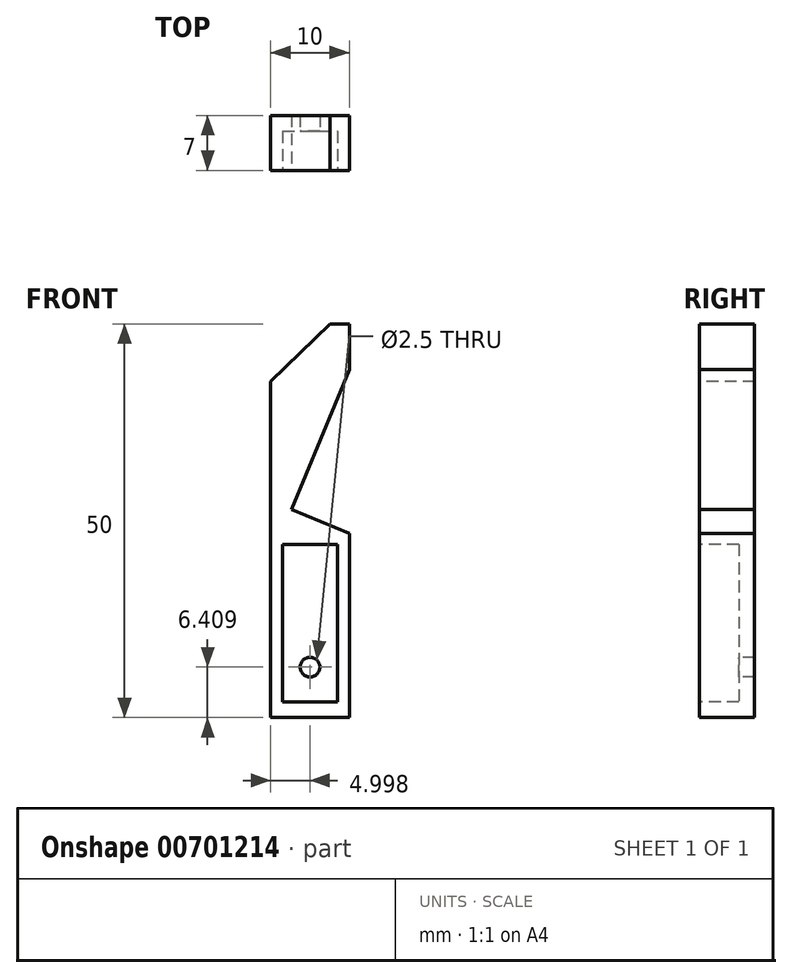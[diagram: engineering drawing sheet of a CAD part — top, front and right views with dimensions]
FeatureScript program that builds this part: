
annotation { "Feature Type Name" : "Feature", "Feature Type Description" : "" }
export const myFeature = defineFeature(function(context is Context, id is Id, definition is map)
    precondition{}
    {
        {
            var Q0;
            Q0=qCreatedBy(makeId("Front.planeOp"),FACE);
            var sketch = newSketch(context, id + "F0", { "sketchPlane" : qUnion([Q0])});
            skLineSegment(sketch, "E0.bottom", {"start": v(-32.17, 52.44) * mm, "end": v(-22.17, 52.44) * mm});
            skLineSegment(sketch, "E0.top", {"start": v(-32.17, 2.44) * mm, "end": v(-22.17, 2.44) * mm});
            skLineSegment(sketch, "E0.left", {"start": v(-32.17, 52.44) * mm, "end": v(-32.17, 2.44) * mm});
            skLineSegment(sketch, "E0.right", {"start": v(-22.17, 52.44) * mm, "end": v(-22.17, 2.44) * mm});
            skSolve(sketch);
        }
        {
            var Q0;
            Q0 = qSketchRegion(id + "F0", true);
            extrude(context, id + "F1", {"entities" : qUnion([Q0]), "depth" : 7 * mm, "offsetDistance" : 25 * mm});
        }
        {
            var Q0;
            Q0=makeQuery(id+"F1.opExtrude","CAP_FACE",FACE,{"disambiguationData":[OSD([sQuery(id+"F0.wireOp",EDGE,"E0.bottom"),sQuery(id+"F0.wireOp",EDGE,"E0.top"),sQuery(id+"F0.wireOp",EDGE,"E0.left"),sQuery(id+"F0.wireOp",EDGE,"E0.right")])],"isStart":false});
            var sketch = newSketch(context, id + "F2", { "sketchPlane" : qUnion([Q0])});
            skLineSegment(sketch, "E1.bottom", {"start": v(-30.67, 24.44) * mm, "end": v(-23.67, 24.44) * mm});
            skLineSegment(sketch, "E1.top", {"start": v(-30.67, 4.44) * mm, "end": v(-23.67, 4.44) * mm});
            skLineSegment(sketch, "E1.left", {"start": v(-30.67, 24.44) * mm, "end": v(-30.67, 4.44) * mm});
            skLineSegment(sketch, "E1.right", {"start": v(-23.67, 24.44) * mm, "end": v(-23.67, 4.44) * mm});
            skSolve(sketch);
        }
        {
            var Q0;
            Q0 = qSketchRegion(id + "F2", true);
            extrude(context, id + "F3", {"entities" : qUnion([Q0]), "operationType" : NewBodyOperationType.REMOVE, "oppositeDirection" : true, "depth" : 5 * mm, "offsetDistance" : 25 * mm});
        }
        {
            var Q0;
            Q0=makeQuery(id+"F3.boolean.opBoolean","COPY",FACE,{"derivedFrom":makeQuery(id+"F3.opExtrude","CAP_FACE",FACE,{"disambiguationData":[OSD([sQuery(id+"F2.wireOp",EDGE,"E1.bottom"),sQuery(id+"F2.wireOp",EDGE,"E1.top"),sQuery(id+"F2.wireOp",EDGE,"E1.left"),sQuery(id+"F2.wireOp",EDGE,"E1.right")])],"isStart":false})});
            var sketch = newSketch(context, id + "F4", { "sketchPlane" : qUnion([Q0])});
            skCircle(sketch, "E2", {"center": v(-27.17, 8.85) * mm, "radius": 1.25 * mm});
            skSolve(sketch);
        }
        {
            var Q0;
            Q0 = qSketchRegion(id + "F4", true);
            extrude(context, id + "F5", {"entities" : qUnion([Q0]), "operationType" : NewBodyOperationType.REMOVE, "endBound" : BoundingType.THROUGH_ALL, "oppositeDirection" : true, "depth" : 25 * mm, "offsetDistance" : 25 * mm});
        }
        {
            var Q0;
            Q0=makeQuery(id+"F1.opExtrude","CAP_FACE",FACE,{"disambiguationData":[OSD([sQuery(id+"F0.wireOp",EDGE,"E0.bottom"),sQuery(id+"F0.wireOp",EDGE,"E0.top"),sQuery(id+"F0.wireOp",EDGE,"E0.left"),sQuery(id+"F0.wireOp",EDGE,"E0.right")])],"isStart":false});
            var sketch = newSketch(context, id + "F6", { "sketchPlane" : qUnion([Q0])});
            skLineSegment(sketch, "E3", {"start": v(-32.17, 45.14) * mm, "end": v(-24.65, 52.44) * mm});
            skLineSegment(sketch, "E4", {"start": v(-32.17, 45.14) * mm, "end": v(-32.17, 52.44) * mm});
            skLineSegment(sketch, "E5", {"start": v(-32.17, 52.44) * mm, "end": v(-24.65, 52.44) * mm});
            skLineSegment(sketch, "E6", {"start": v(-22.17, 25.82) * mm, "end": v(-29.55, 28.89) * mm});
            skLineSegment(sketch, "E7", {"start": v(-29.55, 28.89) * mm, "end": v(-22.17, 46.65) * mm});
            skLineSegment(sketch, "E8", {"start": v(-22.17, 46.65) * mm, "end": v(-22.17, 25.82) * mm});
            skPoint(sketch, "E9", {"position": v(-22.17, 27.44) * mm});
            skSolve(sketch);
        }
        {
            var Q0;
            Q0 = qSketchRegion(id + "F6", true);
            extrude(context, id + "F7", {"entities" : qUnion([Q0]), "operationType" : NewBodyOperationType.REMOVE, "endBound" : BoundingType.THROUGH_ALL, "oppositeDirection" : true, "depth" : 25 * mm, "offsetDistance" : 25 * mm});
        }
    });
